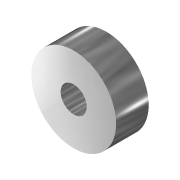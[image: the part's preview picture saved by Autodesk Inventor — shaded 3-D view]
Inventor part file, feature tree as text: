
AUTODESK INVENTOR PART (.ipt)
format: ipt  version: 2022.5 (Build 265521000, 521)  size: 96,768 bytes
history: native  units: mm
features: extrude x1, sketch x1
ambient origin geometry x8: Origin, YZ Plane, XZ Plane, XY Plane, X Axis, Y Axis, Z Axis, Center Point
bodies: Volumenkörper1 (feature_tree)
feature tree (2):
  extrude  "Extrusion1"  Depth=5.0mm
  sketch  "Skizze1"  dims[d0=4.0mm d1=13.0mm d2=5.0mm d3=0.0mm]
